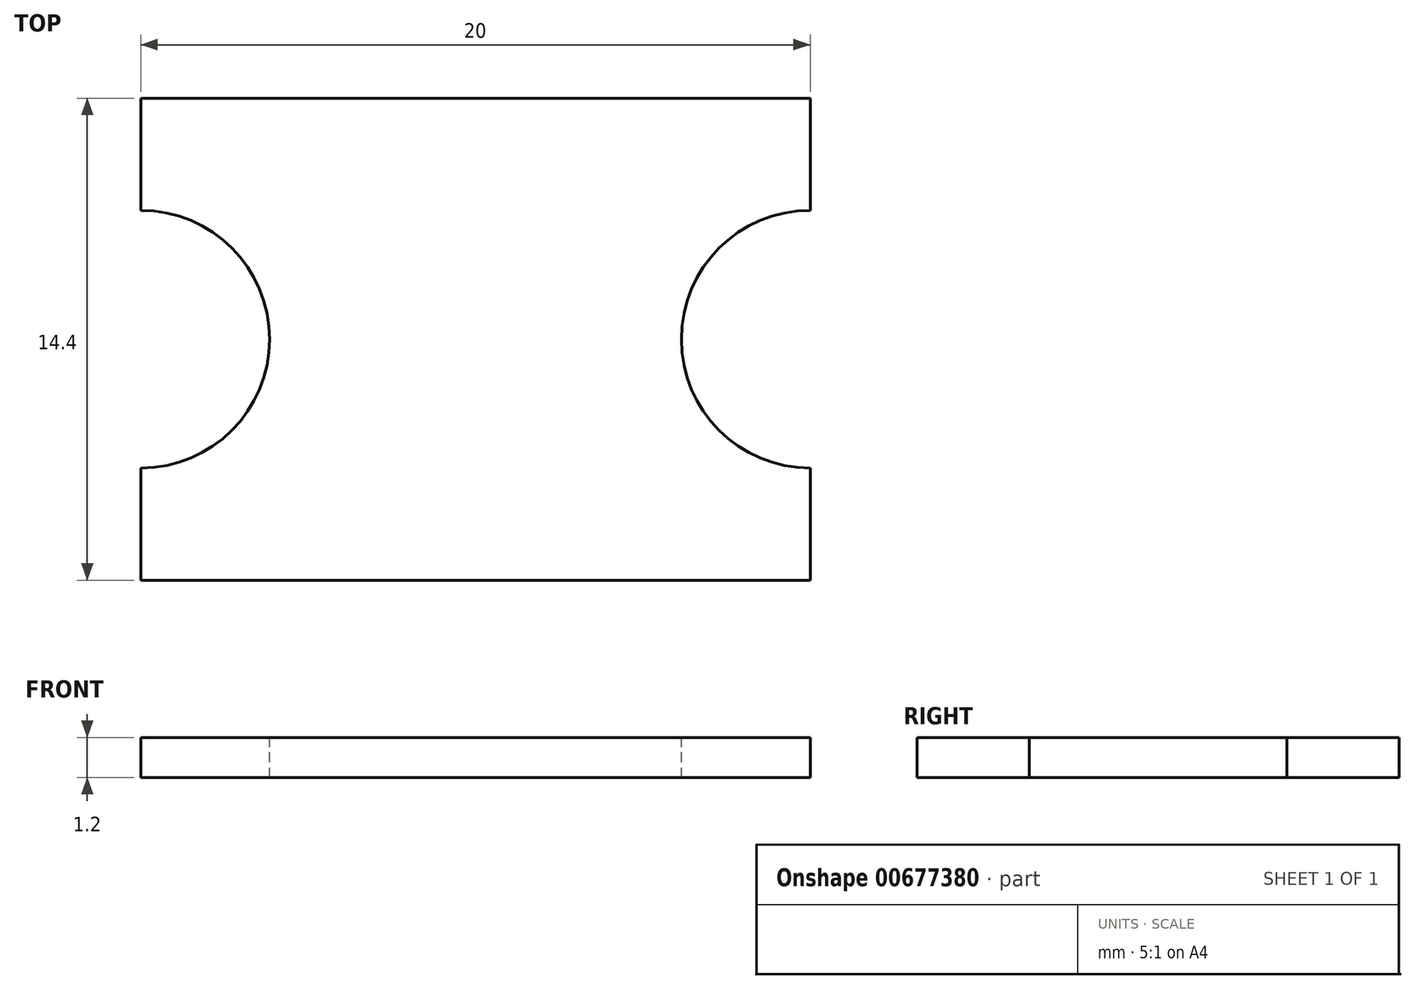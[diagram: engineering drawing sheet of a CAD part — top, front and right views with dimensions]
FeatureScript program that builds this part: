
annotation { "Feature Type Name" : "Feature", "Feature Type Description" : "" }
export const myFeature = defineFeature(function(context is Context, id is Id, definition is map)
    precondition{}
    {
        {
            var Q0;
            Q0=qCreatedBy(makeId("Top.planeOp"),FACE);
            var sketch = newSketch(context, id + "F0", { "sketchPlane" : qUnion([Q0])});
            skLineSegment(sketch, "E0.bottom", {"start": v(-13.44, -0.4) * mm, "end": v(6.56, -0.4) * mm});
            skLineSegment(sketch, "E0.top", {"start": v(-13.44, -14.8) * mm, "end": v(6.56, -14.8) * mm});
            skLineSegment(sketch, "E0.left", {"start": v(-13.44, -0.4) * mm, "end": v(-13.44, -14.8) * mm});
            skLineSegment(sketch, "E0.right", {"start": v(6.56, -0.4) * mm, "end": v(6.56, -14.8) * mm});
            skSolve(sketch);
        }
        {
            var Q0;
            Q0=makeQuery(id+"F0.imprint","IMPRINT",FACE,{"disambiguationData":[TD([[makeQuery(id+"F0.imprint","IMPRINT",EDGE,{"derivedFrom":sQuery(id+"F0.wireOp",EDGE,"E0.bottom")}),-1.0]])]});
            extrude(context, id + "F1", {"entities" : qUnion([Q0]), "depth" : 1.2 * mm, "offsetDistance" : 25.4 * mm});
        }
        {
            var Q0;
            Q0=makeQuery(id+"F1.opExtrude","CAP_FACE",FACE,{"disambiguationData":[OSD([sQuery(id+"F0.wireOp",EDGE,"E0.bottom"),sQuery(id+"F0.wireOp",EDGE,"E0.top"),sQuery(id+"F0.wireOp",EDGE,"E0.left"),sQuery(id+"F0.wireOp",EDGE,"E0.right")])],"isStart":false});
            var sketch = newSketch(context, id + "F2", { "sketchPlane" : qUnion([Q0])});
            skCircle(sketch, "E1", {"center": v(-13.44, -7.6) * mm, "radius": 3.85 * mm});
            skCircle(sketch, "E2", {"center": v(6.56, -7.6) * mm, "radius": 3.85 * mm});
            skSolve(sketch);
        }
        {
            var Q0;
            {var subQ0=sQuery(id+"F2.wireOp",EDGE,"E1");var subQ1=makeQuery(id+"F1.opExtrude","CAP_EDGE",EDGE,{"disambiguationData":[OSD([sQuery(id+"F0.wireOp",EDGE,"E0.left")])],"isStart":false});var subQ2=makeQuery(id+"F2.imprint","INTERSECT",VERTEX,{"disambiguationData":[OD(0.0)],"derivedFrom":[subQ1,subQ0]});Q0=makeQuery(id+"F2.imprint","IMPRINT",FACE,{"disambiguationData":[TD([[makeQuery(id+"F2.imprint","IMPRINT",EDGE,{"disambiguationData":[TD([[subQ2,1.0]])],"derivedFrom":subQ0}),1.0]])]});}
            var Q1;
            {var subQ0=sQuery(id+"F2.wireOp",EDGE,"E2");var subQ1=makeQuery(id+"F1.opExtrude","CAP_EDGE",EDGE,{"disambiguationData":[OSD([sQuery(id+"F0.wireOp",EDGE,"E0.right")])],"isStart":false});var subQ2=makeQuery(id+"F2.imprint","INTERSECT",VERTEX,{"disambiguationData":[OD(0.0)],"derivedFrom":[subQ1,subQ0]});Q1=makeQuery(id+"F2.imprint","IMPRINT",FACE,{"disambiguationData":[TD([[makeQuery(id+"F2.imprint","IMPRINT",EDGE,{"disambiguationData":[TD([[subQ2,-1.0]])],"derivedFrom":subQ0}),1.0]])]});}
            extrude(context, id + "F3", {"entities" : qUnion([Q0, Q1]), "operationType" : NewBodyOperationType.REMOVE, "oppositeDirection" : true, "depth" : 25.4 * mm, "offsetDistance" : 25.4 * mm});
        }
    });
